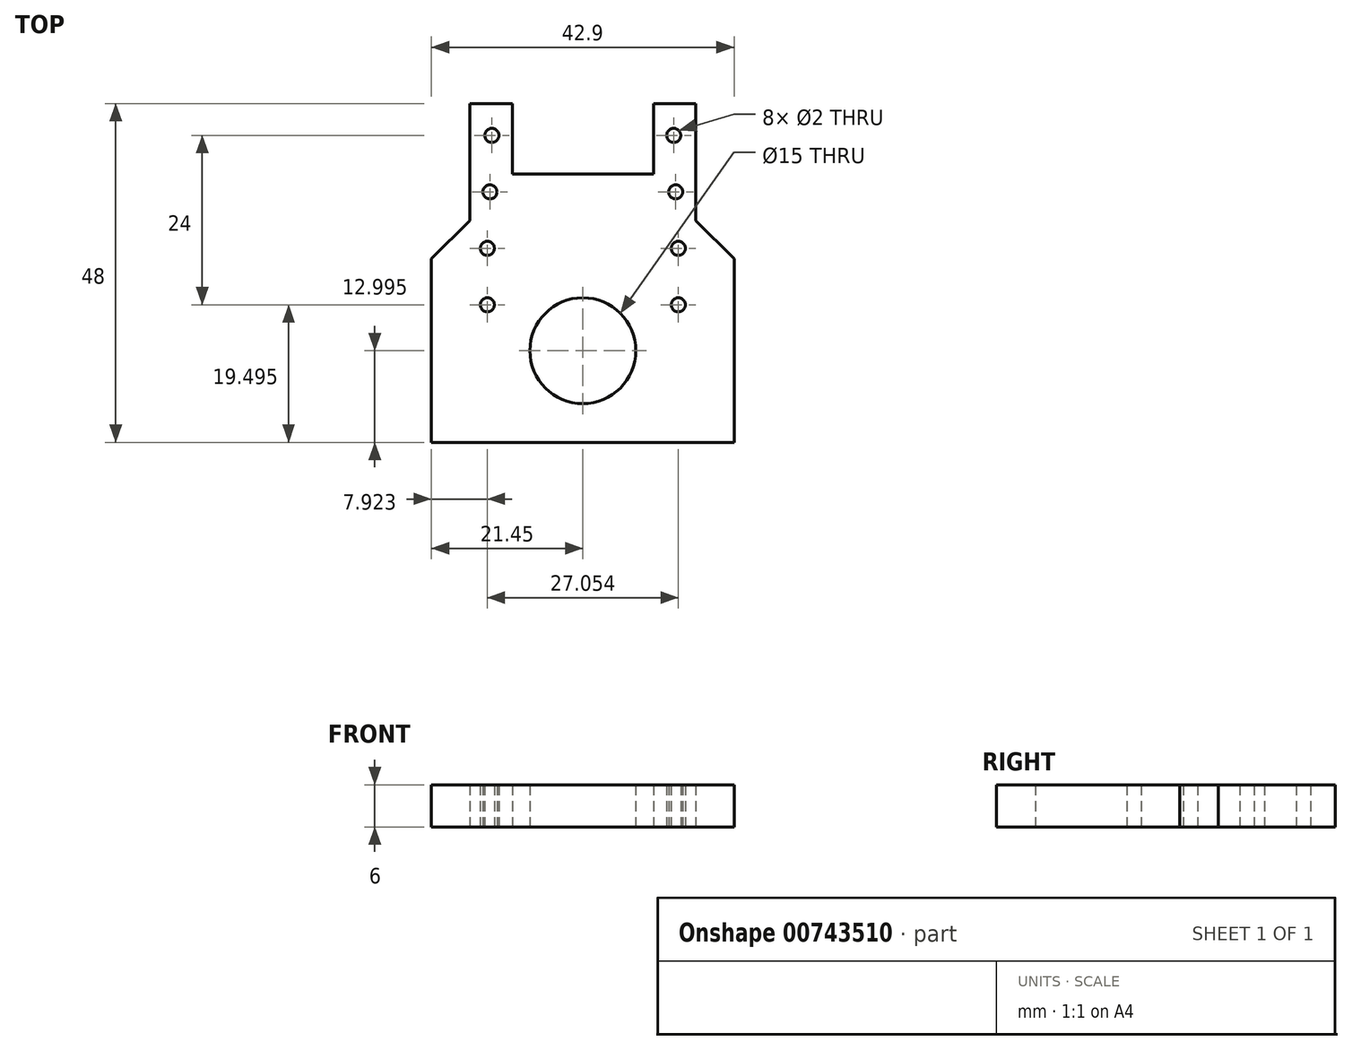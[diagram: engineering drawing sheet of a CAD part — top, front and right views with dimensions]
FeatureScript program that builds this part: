
annotation { "Feature Type Name" : "Feature", "Feature Type Description" : "" }
export const myFeature = defineFeature(function(context is Context, id is Id, definition is map)
    precondition{}
    {
        {
            var Q0;
            Q0=qCreatedBy(makeId("Top.planeOp"),FACE);
            var sketch = newSketch(context, id + "F0", { "sketchPlane" : qUnion([Q0])});
            skLineSegment(sketch, "E0.bottom", {"start": v(-16, 36.18) * mm, "end": v(-10, 36.18) * mm});
            skLineSegment(sketch, "E0.top", {"start": v(-21.45, -11.82) * mm, "end": v(21.45, -11.82) * mm});
            skLineSegment(sketch, "E0.left", {"start": v(-21.45, 14.18) * mm, "end": v(-21.45, -11.82) * mm});
            skLineSegment(sketch, "E0.right", {"start": v(21.45, 14.18) * mm, "end": v(21.45, -11.82) * mm});
            skCircle(sketch, "E1", {"center": v(0, 1.18) * mm, "radius": 7.5 * mm});
            skLineSegment(sketch, "E2.top", {"start": v(-21.45, 14.18) * mm, "end": v(-16, 14.18) * mm, "construction": true});
            skLineSegment(sketch, "E2.right", {"start": v(-16, 36.18) * mm, "end": v(-16, 19.63) * mm});
            skLineSegment(sketch, "E3.top", {"start": v(21.45, 14.18) * mm, "end": v(16, 14.18) * mm, "construction": true});
            skLineSegment(sketch, "E3.right", {"start": v(16, 36.18) * mm, "end": v(16, 19.63) * mm});
            skLineSegment(sketch, "E4", {"start": v(-21.45, 14.18) * mm, "end": v(-16, 19.63) * mm});
            skLineSegment(sketch, "E5", {"start": v(21.45, 14.18) * mm, "end": v(16, 19.63) * mm});
            skLineSegment(sketch, "E6", {"start": v(-16, 19.63) * mm, "end": v(-16, 14.18) * mm, "construction": true});
            skLineSegment(sketch, "E7", {"start": v(16, 19.63) * mm, "end": v(16, 14.18) * mm, "construction": true});
            skCircle(sketch, "E8", {"center": v(-12.89, 31.68) * mm, "radius": 1 * mm});
            skCircle(sketch, "E9", {"center": v(-13.16, 23.68) * mm, "radius": 1 * mm});
            skCircle(sketch, "E10", {"center": v(-13.53, 15.68) * mm, "radius": 1 * mm});
            skLineSegment(sketch, "E11", {"start": v(-10, 36.18) * mm, "end": v(-10, 26.18) * mm});
            skLineSegment(sketch, "E12", {"start": v(-10, 26.18) * mm, "end": v(10, 26.18) * mm});
            skLineSegment(sketch, "E13", {"start": v(10, 26.18) * mm, "end": v(10, 36.18) * mm});
            skLineSegment(sketch, "E14", {"start": v(-10, 36.18) * mm, "end": v(10, 36.18) * mm, "construction": true});
            skLineSegment(sketch, "E15", {"start": v(10, 36.18) * mm, "end": v(16, 36.18) * mm});
            skCircle(sketch, "E16", {"center": v(-13.53, 7.68) * mm, "radius": 1 * mm});
            skCircle(sketch, "E17.MirrorC", {"center": v(12.89, 31.68) * mm, "radius": 1 * mm});
            skCircle(sketch, "E18.MirrorC", {"center": v(13.16, 23.68) * mm, "radius": 1 * mm});
            skCircle(sketch, "E19.MirrorC", {"center": v(13.53, 15.68) * mm, "radius": 1 * mm});
            skCircle(sketch, "E20.MirrorC", {"center": v(13.53, 7.68) * mm, "radius": 1 * mm});
            skSolve(sketch);
        }
        {
            var Q0;
            Q0=qSketchRegion(id+"F0",true);
            extrude(context, id + "F1", {"entities" : qUnion([Q0]), "depth" : 6 * mm});
        }
    });
